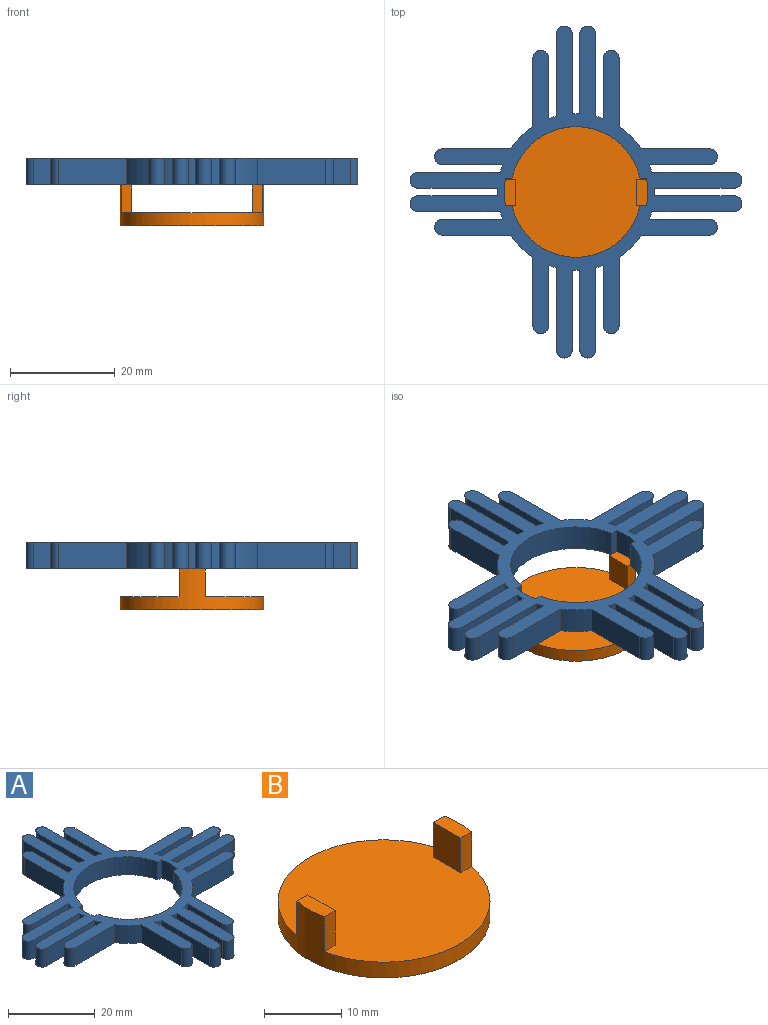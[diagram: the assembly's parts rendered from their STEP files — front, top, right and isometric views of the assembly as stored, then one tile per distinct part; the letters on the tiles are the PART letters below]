
ASSEMBLY  parts=2 mates=1
PART A: 74 faces, bbox 63.5x63.5x5.1 mm
  f0: cylinder r=12.5mm len=24.48mm, axis (0,0,-1), area 172.6mm2, adj f2,f3,f70,f71
  f1: cylinder r=12.5mm len=24.48mm, axis (0,0,-1), area 172.6mm2, adj f2,f3,f68,f73
  f2: plane 63.46x63.46mm, normal (0,0,1), area 922.8mm2, adj f0,f1,f4,f5,f6,f7,f8,f9
  f3: plane 63.46x63.46mm, normal (0,0,-1), area 922.8mm2, adj f0,f1,f4,f5,f6,f7,f8,f9
  f4: cylinder r=1.5mm len=5.05mm, axis (0,0,-1), area 23.8mm2, adj f2,f3,f5,f67
  f5: plane 15.71x5.05mm, normal (0,1,0), area 79.3mm2, adj f2,f3,f4,f6
  f6: cylinder r=15mm len=5.05mm, axis (0,0,-1), area 7.9mm2, adj f2,f3,f5,f7
  f7: plane 11.5x5.05mm, normal (0,-1,0), area 58.1mm2, adj f2,f3,f6,f8
  f8: cylinder r=1.5mm len=5.05mm, axis (0,0,-1), area 23.8mm2, adj f2,f3,f7,f9
  f9: plane 13.02x5.05mm, normal (0,1,0), area 65.8mm2, adj f2,f3,f8,f10
  f10: cylinder r=15mm len=5.05mm, axis (0,0,-1), area 30.8mm2, adj f2,f3,f9,f11
  f11: plane 13.02x5.05mm, normal (1,0,0), area 65.8mm2, adj f2,f3,f10,f12
  f12: cylinder r=1.5mm len=5.05mm, axis (0,0,-1), area 23.8mm2, adj f2,f3,f11,f13
  f13: plane 11.5x5.05mm, normal (-1,0,0), area 58.1mm2, adj f2,f3,f12,f14
  f14: cylinder r=15mm len=5.05mm, axis (0,0,-1), area 7.9mm2, adj f2,f3,f13,f15
  f15: plane 15.71x5.05mm, normal (1,0,0), area 79.3mm2, adj f2,f3,f14,f16
  f16: cylinder r=1.5mm len=5.05mm, axis (0,0,-1), area 23.8mm2, adj f2,f3,f15,f17
  f17: plane 15.25x5.05mm, normal (-1,0,0), area 77mm2, adj f2,f3,f16,f18
  f18: cylinder r=15mm len=5.05mm, axis (0,0,-1), area 7.6mm2, adj f2,f3,f17,f19
  f19: plane 15.25x5.05mm, normal (1,0,0), area 77mm2, adj f2,f3,f18,f20
  f20: cylinder r=1.5mm len=5.05mm, axis (0,0,-1), area 23.8mm2, adj f2,f3,f19,f21
  f21: plane 15.71x5.05mm, normal (-1,0,0), area 79.3mm2, adj f2,f3,f20,f22
  f22: cylinder r=15mm len=5.05mm, axis (0,0,-1), area 7.9mm2, adj f2,f3,f21,f23
  f23: plane 11.5x5.05mm, normal (1,0,0), area 58.1mm2, adj f2,f3,f22,f24
  f24: cylinder r=1.5mm len=5.05mm, axis (0,0,-1), area 23.8mm2, adj f2,f3,f23,f25
  f25: plane 13.02x5.05mm, normal (-1,0,0), area 65.8mm2, adj f2,f3,f24,f26
  f26: cylinder r=15mm len=5.05mm, axis (0,0,-1), area 30.8mm2, adj f2,f3,f25,f27
  f27: plane 13.02x5.05mm, normal (0,1,0), area 65.8mm2, adj f2,f3,f26,f28
  f28: cylinder r=1.5mm len=5.05mm, axis (0,0,-1), area 23.8mm2, adj f2,f3,f27,f29
  f29: plane 11.5x5.05mm, normal (0,-1,0), area 58.1mm2, adj f2,f3,f28,f30
  f30: cylinder r=15mm len=5.05mm, axis (0,0,-1), area 7.9mm2, adj f2,f3,f29,f31
  f31: plane 15.71x5.05mm, normal (0,1,0), area 79.3mm2, adj f2,f3,f30,f32
  f32: cylinder r=1.5mm len=5.05mm, axis (0,0,-1), area 23.8mm2, adj f2,f3,f31,f33
  f33: plane 15.25x5.05mm, normal (0,-1,0), area 77mm2, adj f2,f3,f32,f34
  f34: cylinder r=15mm len=5.05mm, axis (0,0,-1), area 7.6mm2, adj f2,f3,f33,f35
  f35: plane 15.25x5.05mm, normal (0,1,0), area 77mm2, adj f2,f3,f34,f36
  f36: cylinder r=1.5mm len=5.05mm, axis (0,0,-1), area 23.8mm2, adj f2,f3,f35,f37
  f37: plane 15.71x5.05mm, normal (0,-1,0), area 79.3mm2, adj f2,f3,f36,f38
  f38: cylinder r=15mm len=5.05mm, axis (0,0,-1), area 7.9mm2, adj f2,f3,f37,f39
  f39: plane 11.5x5.05mm, normal (0,1,0), area 58.1mm2, adj f2,f3,f38,f40
  f40: cylinder r=1.5mm len=5.05mm, axis (0,0,-1), area 23.8mm2, adj f2,f3,f39,f41
  f41: plane 13.02x5.05mm, normal (0,-1,0), area 65.8mm2, adj f2,f3,f40,f42
  f42: cylinder r=15mm len=5.05mm, axis (0,0,-1), area 30.8mm2, adj f2,f3,f41,f43
  f43: plane 13.02x5.05mm, normal (-1,0,0), area 65.8mm2, adj f2,f3,f42,f44
  f44: cylinder r=1.5mm len=5.05mm, axis (0,0,-1), area 23.8mm2, adj f2,f3,f43,f45
  f45: plane 11.5x5.05mm, normal (1,0,0), area 58.1mm2, adj f2,f3,f44,f46
  f46: cylinder r=15mm len=5.05mm, axis (0,0,-1), area 7.9mm2, adj f2,f3,f45,f47
  f47: plane 15.71x5.05mm, normal (-1,0,0), area 79.3mm2, adj f2,f3,f46,f48
  f48: cylinder r=1.5mm len=5.05mm, axis (0,0,-1), area 23.8mm2, adj f2,f3,f47,f49
  f49: plane 15.25x5.05mm, normal (1,0,0), area 77mm2, adj f2,f3,f48,f50
  f50: cylinder r=15mm len=5.05mm, axis (0,0,-1), area 7.6mm2, adj f2,f3,f49,f51
  f51: plane 15.25x5.05mm, normal (-1,0,0), area 77mm2, adj f2,f3,f50,f52
  f52: cylinder r=1.5mm len=5.05mm, axis (0,0,-1), area 23.8mm2, adj f2,f3,f51,f53
  f53: plane 15.71x5.05mm, normal (1,0,0), area 79.3mm2, adj f2,f3,f52,f54
  f54: cylinder r=15mm len=5.05mm, axis (0,0,-1), area 7.9mm2, adj f2,f3,f53,f55
  f55: plane 11.5x5.05mm, normal (-1,0,0), area 58.1mm2, adj f2,f3,f54,f56
  f56: cylinder r=1.5mm len=5.05mm, axis (0,0,-1), area 23.8mm2, adj f2,f3,f55,f57
  f57: plane 13.02x5.05mm, normal (1,0,0), area 65.8mm2, adj f2,f3,f56,f58
  f58: cylinder r=15mm len=5.05mm, axis (0,0,-1), area 30.8mm2, adj f2,f3,f57,f59
  f59: plane 13.02x5.05mm, normal (0,-1,0), area 65.8mm2, adj f2,f3,f58,f60
  f60: cylinder r=1.5mm len=5.05mm, axis (0,0,-1), area 23.8mm2, adj f2,f3,f59,f61
  f61: plane 11.5x5.05mm, normal (0,1,0), area 58.1mm2, adj f2,f3,f60,f62
  f62: cylinder r=15mm len=5.05mm, axis (0,0,-1), area 7.9mm2, adj f2,f3,f61,f63
  f63: plane 15.71x5.05mm, normal (0,-1,0), area 79.3mm2, adj f2,f3,f62,f64
  f64: cylinder r=1.5mm len=5.05mm, axis (0,0,-1), area 23.8mm2, adj f2,f3,f63,f65
  f65: plane 15.25x5.05mm, normal (0,1,0), area 77mm2, adj f2,f3,f64,f66
  f66: cylinder r=15mm len=5.05mm, axis (0,0,-1), area 7.6mm2, adj f2,f3,f65,f67
  f67: plane 15.25x5.05mm, normal (0,-1,0), area 77mm2, adj f2,f3,f4,f66
  f68: plane 5.05x1.26mm, normal (0,-1,0), area 6.4mm2, adj f1,f2,f3,f69
  f69: cylinder r=13.5mm len=5.05mm, axis (0,0,1), area 25.7mm2, adj f2,f3,f68,f70
  f70: plane 5.05x1.26mm, normal (0,1,0), area 6.4mm2, adj f0,f2,f3,f69
  f71: plane 5.05x1.26mm, normal (0,1,0), area 6.4mm2, adj f0,f2,f3,f72
  f72: cylinder r=13.5mm len=5.05mm, axis (0,0,1), area 25.7mm2, adj f2,f3,f71,f73
  f73: plane 5.05x1.26mm, normal (0,-1,0), area 6.4mm2, adj f1,f2,f3,f72
PART B: 11 faces, bbox 27.5x27.5x8 mm
  f0: plane 27.48x27.03mm, normal (0,0,1), area 571.3mm2, adj f1,f3,f4,f5,f7,f8,f9
  f1: cylinder r=13.74mm len=27.48mm, axis (0,0,-1), area 271.1mm2, adj f0,f2,f3,f4,f6,f7,f9,f10
  f2: plane 27.48x27.48mm, normal (0,0,-1), area 592.9mm2, adj f1
  f3: plane 5.5x2.02mm, normal (0,1,0), area 11.1mm2, adj f0,f1,f5,f6
  f4: plane 5.5x2mm, normal (0,-1,0), area 11mm2, adj f0,f1,f5,f6
  f5: plane 5.5x5mm, normal (1,0,0), area 27.5mm2, adj f0,f3,f4,f6
  f6: plane 5x2.24mm, normal (0,0,1), area 10.8mm2, adj f1,f3,f4,f5
  f7: plane 5.5x2.02mm, normal (0,1,0), area 11.1mm2, adj f0,f1,f8,f10
  f8: plane 5.5x5mm, normal (-1,0,0), area 27.5mm2, adj f0,f7,f9,f10
  f9: plane 5.5x2mm, normal (0,-1,0), area 11mm2, adj f0,f1,f8,f10
  f10: plane 5x2.24mm, normal (0,0,1), area 10.8mm2, adj f1,f7,f8,f9
PLACE A t=(-0.49,1.7,4.53)mm fixed
PLACE B t=(-0.49,1.72,-3.32)mm
MATE slider B.f6 <-> A.f2  axis (0,0,1) through (-13.99,-0.83,4.68)mm
